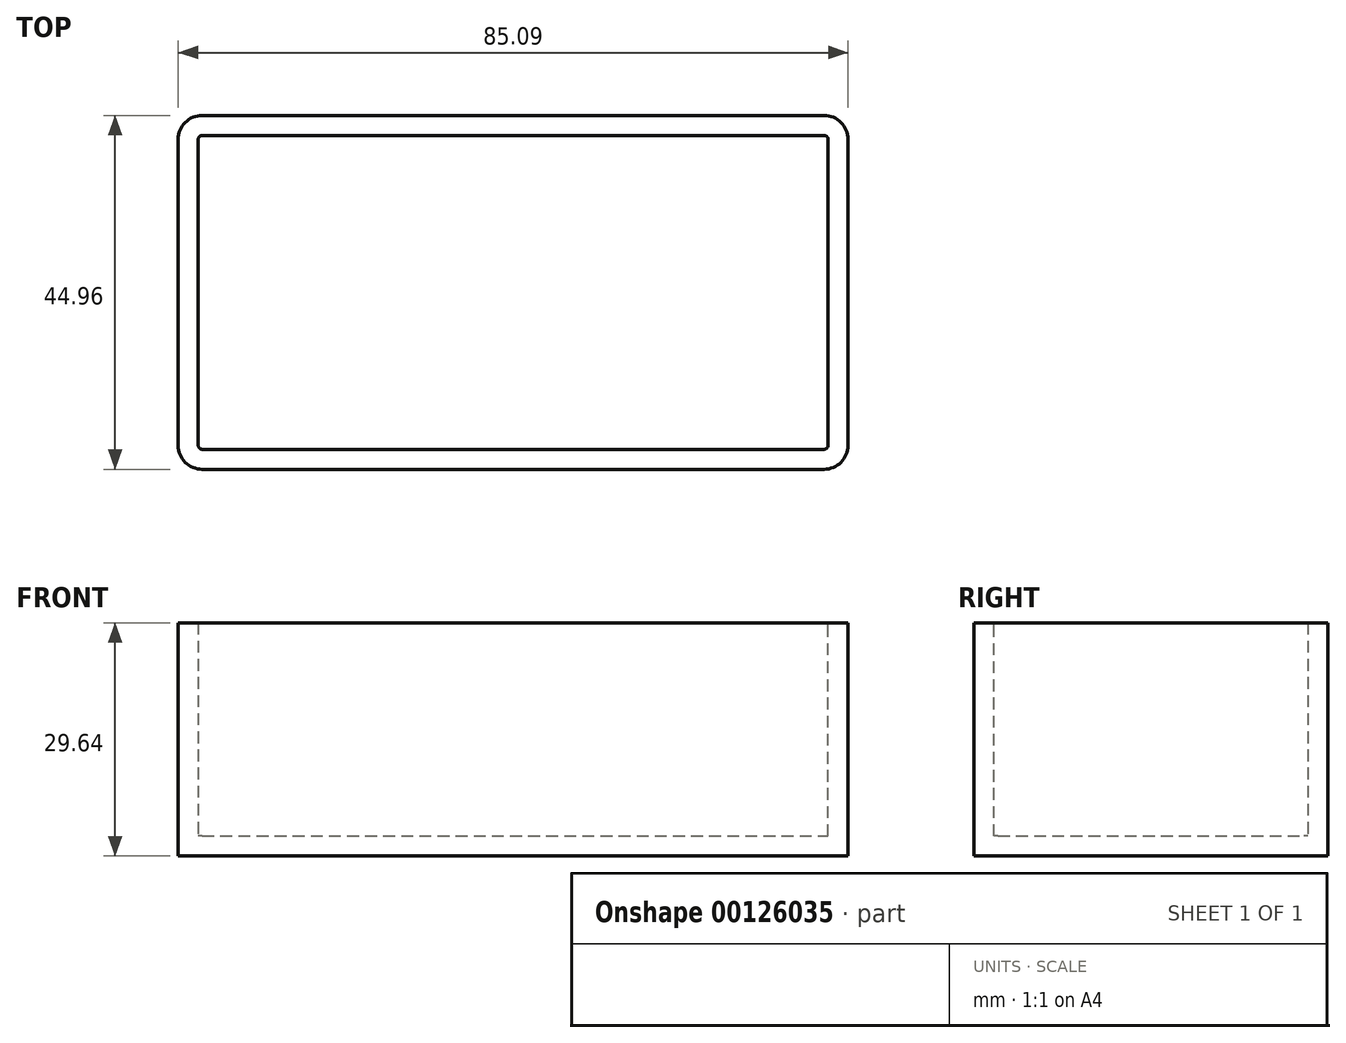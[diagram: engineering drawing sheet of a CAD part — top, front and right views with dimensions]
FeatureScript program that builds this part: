
annotation { "Feature Type Name" : "Feature", "Feature Type Description" : "" }
export const myFeature = defineFeature(function(context is Context, id is Id, definition is map)
    precondition{}
    {
        {
            var Q0;
            Q0=qCreatedBy(makeId("Top.planeOp"),FACE);
            var sketch = newSketch(context, id + "F0", { "sketchPlane" : qUnion([Q0])});
            skLineSegment(sketch, "E0", {"start": v(0, 0) * mm, "end": v(0, 44.96) * mm});
            skLineSegment(sketch, "E1", {"start": v(0, 44.96) * mm, "end": v(-85.1, 44.96) * mm});
            skLineSegment(sketch, "E2", {"start": v(-85.1, 44.96) * mm, "end": v(-85.1, 0) * mm});
            skLineSegment(sketch, "E3", {"start": v(-85.1, 0) * mm, "end": v(0, 0) * mm});
            skSolve(sketch);
        }
        {
            var Q0;
            Q0=makeQuery(id+"F0.imprint","IMPRINT",FACE,{"disambiguationData":[TD([[makeQuery(id+"F0.imprint","IMPRINT",EDGE,{"derivedFrom":sQuery(id+"F0.wireOp",EDGE,"E0")}),1.0]])]});
            extrude(context, id + "F1", {"entities" : qUnion([Q0]), "depth" : 29.64 * mm});
        }
        {
            var Q0;
            Q0=makeQuery(id+"F1.opExtrude","SWEPT_EDGE",EDGE,{"disambiguationData":[OSD([sQuery(id+"F0.wireOp",EDGE,"E1"),sQuery(id+"F0.wireOp",EDGE,"E2")])]});
            var Q1;
            Q1=makeQuery(id+"F1.opExtrude","SWEPT_EDGE",EDGE,{"disambiguationData":[OSD([sQuery(id+"F0.wireOp",EDGE,"E2"),sQuery(id+"F0.wireOp",EDGE,"E3")])]});
            var Q2;
            Q2=makeQuery(id+"F1.opExtrude","SWEPT_EDGE",EDGE,{"disambiguationData":[OSD([sQuery(id+"F0.wireOp",EDGE,"E0"),sQuery(id+"F0.wireOp",EDGE,"E3")])]});
            var Q3;
            Q3=makeQuery(id+"F1.opExtrude","SWEPT_EDGE",EDGE,{"disambiguationData":[OSD([sQuery(id+"F0.wireOp",EDGE,"E0"),sQuery(id+"F0.wireOp",EDGE,"E1")])]});
            fillet(context, id + "F2", {"entities" : qUnion([Q0, Q1, Q2, Q3]), "radius" : 3.05 * mm, "tangentPropagation" : true, "allowEdgeOverflow" : false});
        }
        {
            var Q0;
            Q0=makeQuery(id+"F1.opExtrude","CAP_FACE",FACE,{"disambiguationData":[OSD([sQuery(id+"F0.wireOp",EDGE,"E0"),sQuery(id+"F0.wireOp",EDGE,"E1"),sQuery(id+"F0.wireOp",EDGE,"E2"),sQuery(id+"F0.wireOp",EDGE,"E3")])],"isStart":false});
            shell(context, id + "F3", {"entities" : qUnion([Q0]), "thickness" : 2.54 * mm});
        }
    });
